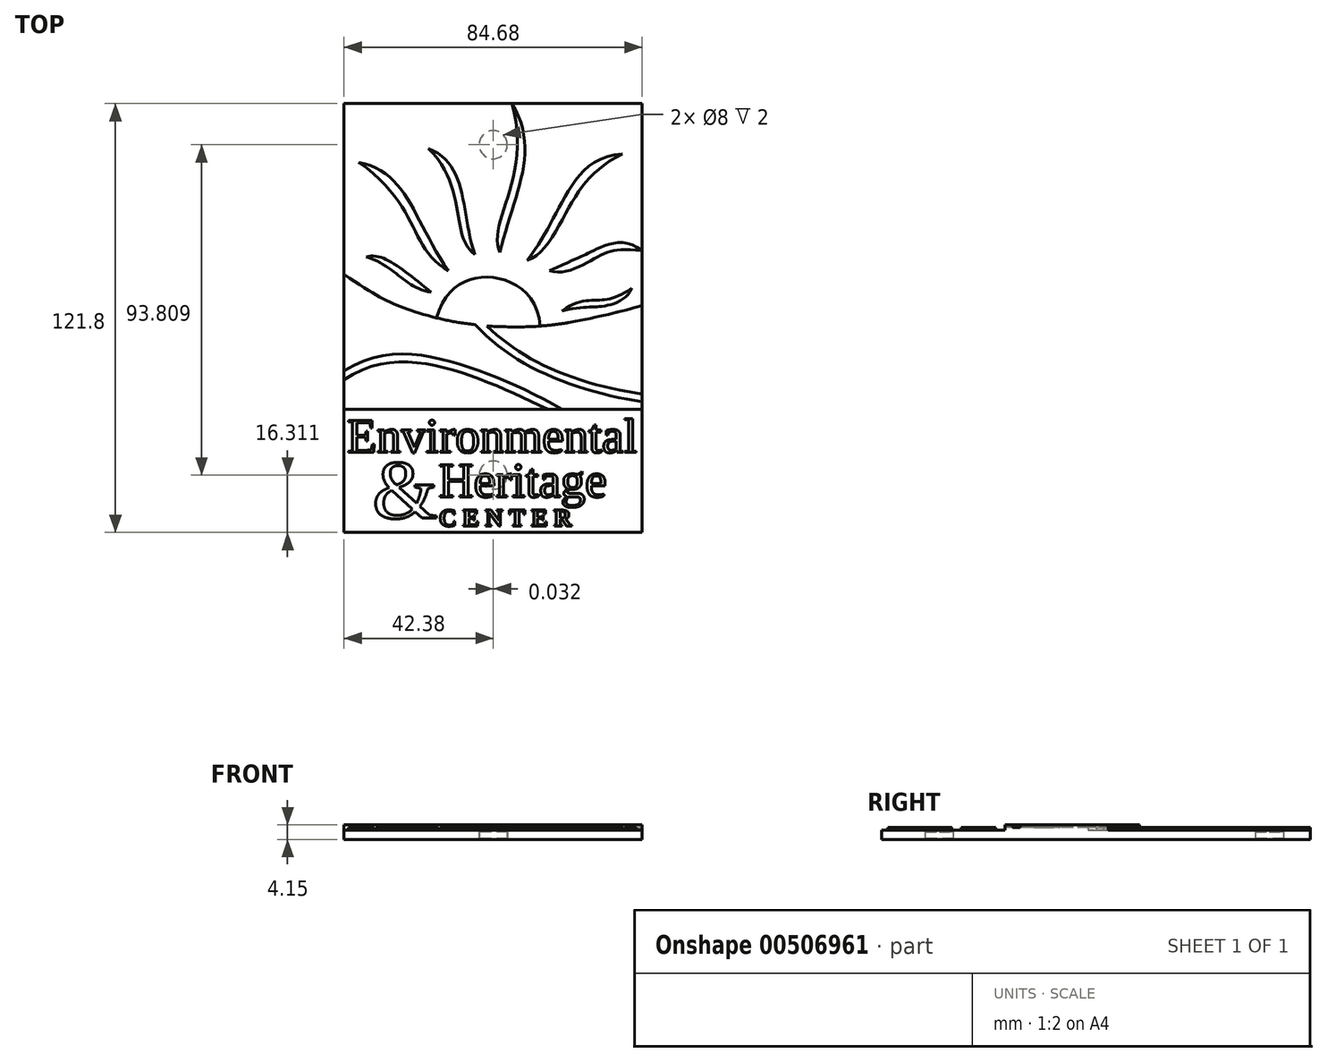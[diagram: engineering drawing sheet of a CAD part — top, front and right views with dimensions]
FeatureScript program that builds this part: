
annotation { "Feature Type Name" : "Feature", "Feature Type Description" : "" }
export const myFeature = defineFeature(function(context is Context, id is Id, definition is map)
    precondition{}
    {
        {
            var Q0;
            Q0=qCreatedBy(makeId("Top.planeOp"),FACE);
            var sketch = newSketch(context, id + "F0", { "sketchPlane" : qUnion([Q0])});
            skFitSpline(sketch, "E0", {"points": [v(8.38, 50.3) * mm, v(5.04, 8) * mm], "startDerivative": vector(25.7, -41) * mm, "endDerivative": vector(-10.42, -47.31) * mm});
            skFitSpline(sketch, "E1", {"points": [v(8.38, 50.3) * mm, v(5.04, 8) * mm], "startDerivative": vector(18.47, -60.9) * mm, "endDerivative": vector(12.18, -25) * mm});
            skFitSpline(sketch, "E2", {"points": [v(-15.3, 37.53) * mm, v(-2.15, 7.39) * mm], "startDerivative": vector(34.1, -13.29) * mm, "endDerivative": vector(12.15, -37.51) * mm});
            skFitSpline(sketch, "E3", {"points": [v(-15.3, 37.53) * mm, v(-2.15, 7.39) * mm], "startDerivative": vector(33.89, -33.1) * mm, "endDerivative": vector(21.74, -16.62) * mm});
            skFitSpline(sketch, "E4", {"points": [v(-35.08, 33.63) * mm, v(-9.6, 2.78) * mm], "startDerivative": vector(41.44, -7.64) * mm, "endDerivative": vector(29.77, -42.85) * mm});
            skFitSpline(sketch, "E5", {"points": [v(-35.08, 33.63) * mm, v(-9.6, 2.78) * mm], "startDerivative": vector(53.11, -37.62) * mm, "endDerivative": vector(34.6, -20.12) * mm});
            skFitSpline(sketch, "E6", {"points": [v(-32.93, 6.81) * mm, v(-14.52, -3.25) * mm], "startDerivative": vector(15.17, 4.31) * mm, "endDerivative": vector(22.51, -17.72) * mm});
            skFitSpline(sketch, "E7", {"points": [v(-32.93, 6.81) * mm, v(-14.52, -3.25) * mm], "startDerivative": vector(24.9, -7.82) * mm, "endDerivative": vector(22.51, -3.35) * mm});
            skFitSpline(sketch, "E8", {"points": [v(39.82, 36.01) * mm, v(22.83, 22.68) * mm, v(12.74, 5.78) * mm], "startDerivative": vector(-55.6, -3.28) * mm, "endDerivative": vector(-26.64, -34.5) * mm});
            skFitSpline(sketch, "E9", {"points": [v(39.82, 36.01) * mm, v(24.83, 21.19) * mm, v(12.74, 5.78) * mm], "startDerivative": vector(-45.9, -23.41) * mm, "endDerivative": vector(-32.14, -10) * mm});
            skFitSpline(sketch, "E10", {"points": [v(19.04, 2.84) * mm, v(30.94, 8.22) * mm, v(45.4, 8.53) * mm], "startDerivative": vector(51.65, 23.48) * mm, "endDerivative": vector(31, -26.2) * mm});
            skFitSpline(sketch, "E11", {"points": [v(19.04, 2.84) * mm, v(32.52, 6.63) * mm, v(45.4, 8.53) * mm], "startDerivative": vector(26.96, -9.36) * mm, "endDerivative": vector(42.76, -4.24) * mm});
            skFitSpline(sketch, "E12", {"points": [v(22.65, -8.56) * mm, v(33.15, -5.52) * mm, v(42.52, -2.16) * mm], "startDerivative": vector(26.71, 19.3) * mm, "endDerivative": vector(25.67, 16.34) * mm});
            skFitSpline(sketch, "E13", {"points": [v(22.65, -8.56) * mm, v(33.85, -7.3) * mm, v(42.52, -2.16) * mm], "startDerivative": vector(37.68, 8.5) * mm, "endDerivative": vector(10.55, 22.66) * mm});
            skFitSpline(sketch, "E14", {"points": [v(1.37, -12.89) * mm, v(18.9, -24.72) * mm, v(45.4, -32.17) * mm], "startDerivative": vector(30.87, -29.73) * mm, "endDerivative": vector(47.12, -6.3) * mm});
            skFitSpline(sketch, "E15", {"points": [v(-1.98, -12.48) * mm, v(18.34, -26.68) * mm, v(45.4, -34.32) * mm], "startDerivative": vector(34.69, -38) * mm, "endDerivative": vector(48.3, -6.34) * mm});
            skFitSpline(sketch, "E16", {"points": [v(1.37, -12.89) * mm, v(22.2, -12.25) * mm, v(45.48, -7.1) * mm], "startDerivative": vector(44.38, -2.18) * mm, "endDerivative": vector(34.77, 9.05) * mm});
            skFitSpline(sketch, "E17", {"points": [v(-39.29, -25.63) * mm, v(-8.43, -23.14) * mm, v(22.66, -36.5) * mm], "startDerivative": vector(63.24, 41.09) * mm, "endDerivative": vector(60.24, -34.22) * mm});
            skFitSpline(sketch, "E18", {"points": [v(-39.29, -28.2) * mm, v(-9.86, -24.95) * mm, v(18.67, -36.5) * mm], "startDerivative": vector(58.5, 40.42) * mm, "endDerivative": vector(56.35, -26.33) * mm});
            skFitSpline(sketch, "E19", {"points": [v(-39.29, 1.8) * mm, v(-21.77, -7.9) * mm, v(-1.98, -12.48) * mm], "startDerivative": vector(51.08, -34.3) * mm, "endDerivative": vector(42.59, -4.16) * mm});
            skFitSpline(sketch, "E20", {"points": [v(-12.98, -10.56) * mm, v(1.97, 1) * mm, v(16.44, -12.88) * mm], "startDerivative": vector(15.1, 52.69) * mm, "endDerivative": vector(3.95, -54.95) * mm});
            skLineSegment(sketch, "E21", {"start": v(-39.29, 50.3) * mm, "end": v(-39.29, -36.5) * mm});
            skLineSegment(sketch, "E22", {"start": v(-39.29, 50.3) * mm, "end": v(45.4, 50.3) * mm});
            skLineSegment(sketch, "E23", {"start": v(-39.29, -36.5) * mm, "end": v(45.4, -36.5) * mm});
            skLineSegment(sketch, "E24.trimOffspring", {"start": v(42.48, 8.76) * mm, "end": v(42.48, 8.78) * mm});
            skLineSegment(sketch, "E25", {"start": v(45.4, 50.3) * mm, "end": v(45.4, -36.5) * mm});
            skText(sketch, "E26", { "text": "Environmental", "fontName": "Tinos-Regular.ttf"});
            skText(sketch, "E27", { "text": "Heritage", "fontName": "Tinos-Regular.ttf"});
            skText(sketch, "E28", { "text": "C E N T E R", "fontName": "Tinos-Bold.ttf"});
            skText(sketch, "E29", { "text": "&", "fontName": "Tinos-Regular.ttf"});
            skLineSegment(sketch, "E30", {"start": v(3.05, 50.3) * mm, "end": v(3.05, -36.5) * mm, "construction": true});
            skLineSegment(sketch, "E31", {"start": v(-39.29, -36.5) * mm, "end": v(-39.29, -71.5) * mm});
            skLineSegment(sketch, "E32", {"start": v(45.4, -36.5) * mm, "end": v(45.4, -71.5) * mm});
            skLineSegment(sketch, "E33", {"start": v(-39.29, -71.5) * mm, "end": v(45.4, -71.5) * mm});
            const initialGuessF0  = {"E26": [-0.0385, -0.04877, 1, 0, 0.01], "E27": [-0.01243, -0.06139, 1, 0, 0.01], "E28": [-0.0123, -0.06969, 1, 0, 0.005], "E29": [-0.0312, -0.06742, 1, 0, 0.01715]};
            skSetInitialGuess(sketch, initialGuessF0);
            skSolve(sketch);
        }
        {
            var Q0;
            Q0 = qSketchRegion(id + "F0", true);
            var Q1;
            Q1=makeQuery(id+"F0.imprint","IMPRINT",FACE,{"disambiguationData":[TD([[makeQuery(id+"F0.imprint","IMPRINT",EDGE,{"derivedFrom":sQuery(id+"F0.wireOp",EDGE,"E6")}),-1.0]])]});
            var Q2;
            Q2=makeQuery(id+"F0.imprint","IMPRINT",FACE,{"disambiguationData":[TD([[makeQuery(id+"F0.imprint","IMPRINT",EDGE,{"derivedFrom":sQuery(id+"F0.wireOp",EDGE,"E4")}),-1.0]])]});
            var Q3;
            Q3=makeQuery(id+"F0.imprint","IMPRINT",FACE,{"disambiguationData":[TD([[makeQuery(id+"F0.imprint","IMPRINT",EDGE,{"derivedFrom":sQuery(id+"F0.wireOp",EDGE,"E2")}),-1.0]])]});
            var Q4;
            Q4=makeQuery(id+"F0.imprint","IMPRINT",FACE,{"disambiguationData":[TD([[makeQuery(id+"F0.imprint","IMPRINT",EDGE,{"derivedFrom":sQuery(id+"F0.wireOp",EDGE,"E8")}),1.0]])]});
            var Q5;
            Q5=makeQuery(id+"F0.imprint","IMPRINT",FACE,{"disambiguationData":[TD([[makeQuery(id+"F0.imprint","IMPRINT",EDGE,{"derivedFrom":sQuery(id+"F0.wireOp",EDGE,"E12")}),-1.0]])]});
            var Q6;
            {var subQ0=sQuery(id+"F0.wireOp",EDGE,"E1");Q6=makeQuery(id+"F0.imprint","IMPRINT",FACE,{"disambiguationData":[TD([[makeQuery(id+"F0.imprint","IMPRINT",EDGE,{"derivedFrom":subQ0}),1.0]])]});}
            var Q7;
            Q7=makeQuery(id+"F0.imprint","IMPRINT",FACE,{"disambiguationData":[TD([[makeQuery(id+"F0.imprint","IMPRINT",EDGE,{"derivedFrom":sQuery(id+"F0.wireOp",EDGE,"E29.sketch_text.stroke-28")}),1.0]])]});
            var Q8;
            Q8=makeQuery(id+"F0.imprint","IMPRINT",FACE,{"disambiguationData":[TD([[makeQuery(id+"F0.imprint","IMPRINT",EDGE,{"derivedFrom":sQuery(id+"F0.wireOp",EDGE,"E26.sketch_text.stroke-0")}),-1.0]])]});
            var Q9;
            Q9=makeQuery(id+"F0.imprint","IMPRINT",FACE,{"disambiguationData":[TD([[makeQuery(id+"F0.imprint","IMPRINT",EDGE,{"derivedFrom":sQuery(id+"F0.wireOp",EDGE,"E26.sketch_text.stroke-26")}),-1.0]])]});
            var Q10;
            Q10=makeQuery(id+"F0.imprint","IMPRINT",FACE,{"disambiguationData":[TD([[makeQuery(id+"F0.imprint","IMPRINT",EDGE,{"derivedFrom":sQuery(id+"F0.wireOp",EDGE,"E26.sketch_text.stroke-51")}),-1.0]])]});
            var Q11;
            Q11=makeQuery(id+"F0.imprint","IMPRINT",FACE,{"disambiguationData":[TD([[makeQuery(id+"F0.imprint","IMPRINT",EDGE,{"derivedFrom":sQuery(id+"F0.wireOp",EDGE,"E26.sketch_text.stroke-74")}),-1.0]])]});
            var Q12;
            Q12=makeQuery(id+"F0.imprint","IMPRINT",FACE,{"disambiguationData":[TD([[makeQuery(id+"F0.imprint","IMPRINT",EDGE,{"derivedFrom":sQuery(id+"F0.wireOp",EDGE,"E26.sketch_text.stroke-84")}),-1.0]])]});
            var Q13;
            Q13=makeQuery(id+"F0.imprint","IMPRINT",FACE,{"disambiguationData":[TD([[makeQuery(id+"F0.imprint","IMPRINT",EDGE,{"derivedFrom":sQuery(id+"F0.wireOp",EDGE,"E26.sketch_text.stroke-103")}),-1.0]])]});
            var Q14;
            Q14=makeQuery(id+"F0.imprint","IMPRINT",FACE,{"disambiguationData":[TD([[makeQuery(id+"F0.imprint","IMPRINT",EDGE,{"derivedFrom":sQuery(id+"F0.wireOp",EDGE,"E26.sketch_text.stroke-110")}),1.0]])]});
            var Q15;
            Q15=makeQuery(id+"F0.imprint","IMPRINT",FACE,{"disambiguationData":[TD([[makeQuery(id+"F0.imprint","IMPRINT",EDGE,{"derivedFrom":sQuery(id+"F0.wireOp",EDGE,"E26.sketch_text.stroke-118")}),-1.0]])]});
            var Q16;
            Q16=makeQuery(id+"F0.imprint","IMPRINT",FACE,{"disambiguationData":[TD([[makeQuery(id+"F0.imprint","IMPRINT",EDGE,{"derivedFrom":sQuery(id+"F0.wireOp",EDGE,"E26.sketch_text.stroke-143")}),-1.0]])]});
            var Q17;
            Q17=makeQuery(id+"F0.imprint","IMPRINT",FACE,{"disambiguationData":[TD([[makeQuery(id+"F0.imprint","IMPRINT",EDGE,{"derivedFrom":sQuery(id+"F0.wireOp",EDGE,"E27.sketch_text.stroke-49")}),-1.0]])]});
            var Q18;
            Q18=makeQuery(id+"F0.imprint","IMPRINT",FACE,{"disambiguationData":[TD([[makeQuery(id+"F0.imprint","IMPRINT",EDGE,{"derivedFrom":sQuery(id+"F0.wireOp",EDGE,"E27.sketch_text.stroke-28")}),-1.0]])]});
            var Q19;
            Q19=makeQuery(id+"F0.imprint","IMPRINT",FACE,{"disambiguationData":[TD([[makeQuery(id+"F0.imprint","IMPRINT",EDGE,{"derivedFrom":sQuery(id+"F0.wireOp",EDGE,"E27.sketch_text.stroke-44")}),1.0]])]});
            var Q20;
            Q20=makeQuery(id+"F0.imprint","IMPRINT",FACE,{"disambiguationData":[TD([[makeQuery(id+"F0.imprint","IMPRINT",EDGE,{"derivedFrom":sQuery(id+"F0.wireOp",EDGE,"E27.sketch_text.stroke-0")}),-1.0]])]});
            var Q21;
            Q21=makeQuery(id+"F0.imprint","IMPRINT",FACE,{"disambiguationData":[TD([[makeQuery(id+"F0.imprint","IMPRINT",EDGE,{"derivedFrom":sQuery(id+"F0.wireOp",EDGE,"E29.sketch_text.stroke-0")}),-1.0]])]});
            var Q22;
            Q22=makeQuery(id+"F0.imprint","IMPRINT",FACE,{"disambiguationData":[TD([[makeQuery(id+"F0.imprint","IMPRINT",EDGE,{"derivedFrom":sQuery(id+"F0.wireOp",EDGE,"E29.sketch_text.stroke-34")}),1.0]])]});
            var Q23;
            Q23=makeQuery(id+"F0.imprint","IMPRINT",FACE,{"disambiguationData":[TD([[makeQuery(id+"F0.imprint","IMPRINT",EDGE,{"derivedFrom":sQuery(id+"F0.wireOp",EDGE,"E28.sketch_text.stroke-0")}),-1.0]])]});
            var Q24;
            Q24=makeQuery(id+"F0.imprint","IMPRINT",FACE,{"disambiguationData":[TD([[makeQuery(id+"F0.imprint","IMPRINT",EDGE,{"derivedFrom":sQuery(id+"F0.wireOp",EDGE,"E28.sketch_text.stroke-20")}),-1.0]])]});
            var Q25;
            Q25=makeQuery(id+"F0.imprint","IMPRINT",FACE,{"disambiguationData":[TD([[makeQuery(id+"F0.imprint","IMPRINT",EDGE,{"derivedFrom":sQuery(id+"F0.wireOp",EDGE,"E28.sketch_text.stroke-46")}),-1.0]])]});
            var Q26;
            Q26=makeQuery(id+"F0.imprint","IMPRINT",FACE,{"disambiguationData":[TD([[makeQuery(id+"F0.imprint","IMPRINT",EDGE,{"derivedFrom":sQuery(id+"F0.wireOp",EDGE,"E28.sketch_text.stroke-66")}),-1.0]])]});
            var Q27;
            Q27=makeQuery(id+"F0.imprint","IMPRINT",FACE,{"disambiguationData":[TD([[makeQuery(id+"F0.imprint","IMPRINT",EDGE,{"derivedFrom":sQuery(id+"F0.wireOp",EDGE,"E27.sketch_text.stroke-76")}),-1.0]])]});
            var Q28;
            Q28=makeQuery(id+"F0.imprint","IMPRINT",FACE,{"disambiguationData":[TD([[makeQuery(id+"F0.imprint","IMPRINT",EDGE,{"derivedFrom":sQuery(id+"F0.wireOp",EDGE,"E27.sketch_text.stroke-68")}),-1.0]])]});
            var Q29;
            Q29=makeQuery(id+"F0.imprint","IMPRINT",FACE,{"disambiguationData":[TD([[makeQuery(id+"F0.imprint","IMPRINT",EDGE,{"derivedFrom":sQuery(id+"F0.wireOp",EDGE,"E26.sketch_text.stroke-66")}),-1.0]])]});
            var Q30;
            Q30=makeQuery(id+"F0.imprint","IMPRINT",FACE,{"disambiguationData":[TD([[makeQuery(id+"F0.imprint","IMPRINT",EDGE,{"derivedFrom":sQuery(id+"F0.wireOp",EDGE,"E26.sketch_text.stroke-184")}),-1.0]])]});
            var Q31;
            Q31=makeQuery(id+"F0.imprint","IMPRINT",FACE,{"disambiguationData":[TD([[makeQuery(id+"F0.imprint","IMPRINT",EDGE,{"derivedFrom":sQuery(id+"F0.wireOp",EDGE,"E26.sketch_text.stroke-200")}),1.0]])]});
            var Q32;
            Q32=makeQuery(id+"F0.imprint","IMPRINT",FACE,{"disambiguationData":[TD([[makeQuery(id+"F0.imprint","IMPRINT",EDGE,{"derivedFrom":sQuery(id+"F0.wireOp",EDGE,"E26.sketch_text.stroke-205")}),-1.0]])]});
            var Q33;
            Q33=makeQuery(id+"F0.imprint","IMPRINT",FACE,{"disambiguationData":[TD([[makeQuery(id+"F0.imprint","IMPRINT",EDGE,{"derivedFrom":sQuery(id+"F0.wireOp",EDGE,"E26.sketch_text.stroke-230")}),-1.0]])]});
            var Q34;
            Q34=makeQuery(id+"F0.imprint","IMPRINT",FACE,{"disambiguationData":[TD([[makeQuery(id+"F0.imprint","IMPRINT",EDGE,{"derivedFrom":sQuery(id+"F0.wireOp",EDGE,"E26.sketch_text.stroke-270")}),1.0]])]});
            var Q35;
            Q35=makeQuery(id+"F0.imprint","IMPRINT",FACE,{"disambiguationData":[TD([[makeQuery(id+"F0.imprint","IMPRINT",EDGE,{"derivedFrom":sQuery(id+"F0.wireOp",EDGE,"E26.sketch_text.stroke-249")}),-1.0]])]});
            var Q36;
            Q36=makeQuery(id+"F0.imprint","IMPRINT",FACE,{"disambiguationData":[TD([[makeQuery(id+"F0.imprint","IMPRINT",EDGE,{"derivedFrom":sQuery(id+"F0.wireOp",EDGE,"E26.sketch_text.stroke-277")}),-1.0]])]});
            var Q37;
            Q37=makeQuery(id+"F0.imprint","IMPRINT",FACE,{"disambiguationData":[TD([[makeQuery(id+"F0.imprint","IMPRINT",EDGE,{"derivedFrom":sQuery(id+"F0.wireOp",EDGE,"E27.sketch_text.stroke-178")}),-1.0]])]});
            var Q38;
            Q38=makeQuery(id+"F0.imprint","IMPRINT",FACE,{"disambiguationData":[TD([[makeQuery(id+"F0.imprint","IMPRINT",EDGE,{"derivedFrom":sQuery(id+"F0.wireOp",EDGE,"E27.sketch_text.stroke-194")}),1.0]])]});
            var Q39;
            Q39=makeQuery(id+"F0.imprint","IMPRINT",FACE,{"disambiguationData":[TD([[makeQuery(id+"F0.imprint","IMPRINT",EDGE,{"derivedFrom":sQuery(id+"F0.wireOp",EDGE,"E27.sketch_text.stroke-133")}),-1.0]])]});
            var Q40;
            Q40=makeQuery(id+"F0.imprint","IMPRINT",FACE,{"disambiguationData":[TD([[makeQuery(id+"F0.imprint","IMPRINT",EDGE,{"derivedFrom":sQuery(id+"F0.wireOp",EDGE,"E27.sketch_text.stroke-170")}),1.0]])]});
            var Q41;
            Q41=makeQuery(id+"F0.imprint","IMPRINT",FACE,{"disambiguationData":[TD([[makeQuery(id+"F0.imprint","IMPRINT",EDGE,{"derivedFrom":sQuery(id+"F0.wireOp",EDGE,"E27.sketch_text.stroke-161")}),1.0]])]});
            var Q42;
            Q42=makeQuery(id+"F0.imprint","IMPRINT",FACE,{"disambiguationData":[TD([[makeQuery(id+"F0.imprint","IMPRINT",EDGE,{"derivedFrom":sQuery(id+"F0.wireOp",EDGE,"E27.sketch_text.stroke-126")}),1.0]])]});
            var Q43;
            Q43=makeQuery(id+"F0.imprint","IMPRINT",FACE,{"disambiguationData":[TD([[makeQuery(id+"F0.imprint","IMPRINT",EDGE,{"derivedFrom":sQuery(id+"F0.wireOp",EDGE,"E27.sketch_text.stroke-105")}),-1.0]])]});
            var Q44;
            Q44=makeQuery(id+"F0.imprint","IMPRINT",FACE,{"disambiguationData":[TD([[makeQuery(id+"F0.imprint","IMPRINT",EDGE,{"derivedFrom":sQuery(id+"F0.wireOp",EDGE,"E27.sketch_text.stroke-86")}),-1.0]])]});
            var Q45;
            Q45=makeQuery(id+"F0.imprint","IMPRINT",FACE,{"disambiguationData":[TD([[makeQuery(id+"F0.imprint","IMPRINT",EDGE,{"derivedFrom":sQuery(id+"F0.wireOp",EDGE,"E28.sketch_text.stroke-84")}),-1.0]])]});
            var Q46;
            Q46=makeQuery(id+"F0.imprint","IMPRINT",FACE,{"disambiguationData":[TD([[makeQuery(id+"F0.imprint","IMPRINT",EDGE,{"derivedFrom":sQuery(id+"F0.wireOp",EDGE,"E28.sketch_text.stroke-110")}),-1.0]])]});
            var Q47;
            Q47=makeQuery(id+"F0.imprint","IMPRINT",FACE,{"disambiguationData":[TD([[makeQuery(id+"F0.imprint","IMPRINT",EDGE,{"derivedFrom":sQuery(id+"F0.wireOp",EDGE,"E28.sketch_text.stroke-129")}),1.0]])]});
            extrude(context, id + "F1", {"entities" : qUnion([Q0, Q1, Q2, Q3, Q4, Q5, Q6, Q7, Q8, Q9, Q10, Q11, Q12, Q13, Q14, Q15, Q16, Q17, Q18, Q19, Q20, Q21, Q22, Q23, Q24, Q25, Q26, Q27, Q28, Q29, Q30, Q31, Q32, Q33, Q34, Q35, Q36, Q37, Q38, Q39, Q40, Q41, Q42, Q43, Q44, Q45, Q46, Q47]), "depth" : 2.55 * mm, "offsetDistance" : 25 * mm});
        }
        {
            var Q0;
            Q0=makeQuery(id+"F1.opExtrude","CAP_FACE",FACE,{"disambiguationData":[OSD([sQuery(id+"F0.wireOp",EDGE,"E21"),sQuery(id+"F0.wireOp",EDGE,"E22"),sQuery(id+"F0.wireOp",EDGE,"E25"),sQuery(id+"F0.wireOp",EDGE,"E31"),sQuery(id+"F0.wireOp",EDGE,"E32"),sQuery(id+"F0.wireOp",EDGE,"E33")])],"isStart":false});
            var sketch = newSketch(context, id + "F2", { "sketchPlane" : qUnion([Q0])});
            skFitSpline(sketch, "E34", {"points": [v(8.38, 50.3) * mm, v(5.04, 8) * mm], "startDerivative": vector(25.7, -41) * mm, "endDerivative": vector(-10.42, -47.31) * mm});
            skFitSpline(sketch, "E35", {"points": [v(8.38, 50.3) * mm, v(5.04, 8) * mm], "startDerivative": vector(18.47, -60.9) * mm, "endDerivative": vector(12.18, -25) * mm});
            skFitSpline(sketch, "E36", {"points": [v(-15.3, 37.53) * mm, v(-2.15, 7.39) * mm], "startDerivative": vector(34.1, -13.29) * mm, "endDerivative": vector(12.15, -37.51) * mm});
            skFitSpline(sketch, "E37", {"points": [v(-15.3, 37.53) * mm, v(-2.15, 7.39) * mm], "startDerivative": vector(33.89, -33.1) * mm, "endDerivative": vector(21.74, -16.62) * mm});
            skFitSpline(sketch, "E38", {"points": [v(-35.08, 33.63) * mm, v(-9.6, 2.78) * mm], "startDerivative": vector(41.44, -7.64) * mm, "endDerivative": vector(29.77, -42.85) * mm});
            skFitSpline(sketch, "E39", {"points": [v(-35.08, 33.63) * mm, v(-9.6, 2.78) * mm], "startDerivative": vector(53.11, -37.62) * mm, "endDerivative": vector(34.6, -20.12) * mm});
            skFitSpline(sketch, "E40", {"points": [v(-32.93, 6.81) * mm, v(-14.52, -3.25) * mm], "startDerivative": vector(15.17, 4.31) * mm, "endDerivative": vector(22.51, -17.72) * mm});
            skFitSpline(sketch, "E41", {"points": [v(-32.93, 6.81) * mm, v(-14.52, -3.25) * mm], "startDerivative": vector(24.9, -7.82) * mm, "endDerivative": vector(22.51, -3.35) * mm});
            skFitSpline(sketch, "E42", {"points": [v(39.82, 36.01) * mm, v(22.83, 22.68) * mm, v(12.74, 5.78) * mm], "startDerivative": vector(-55.6, -3.28) * mm, "endDerivative": vector(-26.64, -34.5) * mm});
            skFitSpline(sketch, "E43", {"points": [v(39.82, 36.01) * mm, v(24.83, 21.19) * mm, v(12.74, 5.78) * mm], "startDerivative": vector(-45.9, -23.41) * mm, "endDerivative": vector(-32.14, -10) * mm});
            skFitSpline(sketch, "E44", {"points": [v(19.04, 2.84) * mm, v(30.94, 8.22) * mm, v(45.38, 8.52) * mm], "startDerivative": vector(51.65, 23.48) * mm, "endDerivative": vector(31, -26.2) * mm});
            skFitSpline(sketch, "E45", {"points": [v(19.04, 2.84) * mm, v(32.52, 6.63) * mm, v(45.38, 8.53) * mm], "startDerivative": vector(26.96, -9.36) * mm, "endDerivative": vector(42.76, -4.23) * mm});
            skFitSpline(sketch, "E46", {"points": [v(22.65, -8.56) * mm, v(33.15, -5.52) * mm, v(42.52, -2.16) * mm], "startDerivative": vector(26.71, 19.3) * mm, "endDerivative": vector(25.67, 16.34) * mm});
            skFitSpline(sketch, "E47", {"points": [v(22.65, -8.56) * mm, v(33.85, -7.3) * mm, v(42.52, -2.16) * mm], "startDerivative": vector(37.68, 8.5) * mm, "endDerivative": vector(10.55, 22.66) * mm});
            skFitSpline(sketch, "E48", {"points": [v(1.37, -12.89) * mm, v(18.9, -24.72) * mm, v(45.4, -32.17) * mm], "startDerivative": vector(30.87, -29.73) * mm, "endDerivative": vector(47.12, -6.3) * mm});
            skFitSpline(sketch, "E49", {"points": [v(-1.98, -12.48) * mm, v(18.34, -26.68) * mm, v(45.4, -34.32) * mm], "startDerivative": vector(34.69, -38) * mm, "endDerivative": vector(48.3, -6.34) * mm});
            skFitSpline(sketch, "E50", {"points": [v(1.37, -12.89) * mm, v(22.2, -12.25) * mm, v(45.48, -7.1) * mm], "startDerivative": vector(44.38, -2.18) * mm, "endDerivative": vector(34.77, 9.05) * mm});
            skFitSpline(sketch, "E51", {"points": [v(-39.29, -25.63) * mm, v(-8.43, -23.14) * mm, v(22.66, -36.5) * mm], "startDerivative": vector(63.24, 41.09) * mm, "endDerivative": vector(60.24, -34.22) * mm});
            skFitSpline(sketch, "E52", {"points": [v(-39.29, -28.2) * mm, v(-9.86, -24.95) * mm, v(18.67, -36.5) * mm], "startDerivative": vector(58.5, 40.42) * mm, "endDerivative": vector(56.35, -26.33) * mm});
            skFitSpline(sketch, "E53", {"points": [v(-39.29, 1.8) * mm, v(-21.77, -7.9) * mm, v(-1.98, -12.48) * mm], "startDerivative": vector(51.08, -34.3) * mm, "endDerivative": vector(42.59, -4.16) * mm});
            skFitSpline(sketch, "E54", {"points": [v(-12.98, -10.56) * mm, v(1.97, 1) * mm, v(16.44, -12.88) * mm], "startDerivative": vector(15.1, 52.69) * mm, "endDerivative": vector(3.95, -54.95) * mm});
            skLineSegment(sketch, "E55", {"start": v(-39.29, 50.3) * mm, "end": v(-39.29, -36.5) * mm});
            skLineSegment(sketch, "E56", {"start": v(-39.29, 50.3) * mm, "end": v(45.4, 50.3) * mm});
            skLineSegment(sketch, "E57", {"start": v(-39.29, -36.5) * mm, "end": v(45.4, -36.5) * mm});
            skLineSegment(sketch, "E58.trimOffspring", {"start": v(42.48, 8.76) * mm, "end": v(42.48, 8.78) * mm});
            skLineSegment(sketch, "E59", {"start": v(45.4, 50.3) * mm, "end": v(45.4, -36.5) * mm});
            skText(sketch, "E60", { "text": "Environmental", "fontName": "Tinos-Regular.ttf"});
            skText(sketch, "E61", { "text": "Heritage", "fontName": "Tinos-Regular.ttf"});
            skText(sketch, "E62", { "text": "C E N T E R", "fontName": "Tinos-Bold.ttf"});
            skText(sketch, "E63", { "text": "&", "fontName": "Tinos-Regular.ttf"});
            skLineSegment(sketch, "E64", {"start": v(3.05, 50.3) * mm, "end": v(3.05, -36.5) * mm, "construction": true});
            skLineSegment(sketch, "E65", {"start": v(-39.29, -36.5) * mm, "end": v(-39.29, -71.5) * mm});
            skLineSegment(sketch, "E66", {"start": v(45.4, -36.5) * mm, "end": v(45.4, -71.5) * mm});
            skLineSegment(sketch, "E67", {"start": v(-39.29, -71.5) * mm, "end": v(45.4, -71.5) * mm});
            const initialGuessF2  = {"E60": [-0.0385, -0.04877, 1, 0, 0.01], "E61": [-0.01243, -0.06139, 1, 0, 0.01], "E62": [-0.0123, -0.06969, 1, 0, 0.005], "E63": [-0.0312, -0.06742, 1, 0, 0.01715]};
            skSetInitialGuess(sketch, initialGuessF2);
            skSolve(sketch);
        }
        {
            var Q0;
            Q0=makeQuery(id+"F2.imprint","IMPRINT",FACE,{"disambiguationData":[TD([[makeQuery(id+"F2.imprint","IMPRINT",EDGE,{"derivedFrom":sQuery(id+"F2.wireOp",EDGE,"E60.sketch_text.stroke-205")}),-1.0]])]});
            var Q1;
            Q1=makeQuery(id+"F2.imprint","IMPRINT",FACE,{"disambiguationData":[TD([[makeQuery(id+"F2.imprint","IMPRINT",EDGE,{"derivedFrom":sQuery(id+"F2.wireOp",EDGE,"E60.sketch_text.stroke-184")}),-1.0]])]});
            var Q2;
            Q2=makeQuery(id+"F2.imprint","IMPRINT",FACE,{"disambiguationData":[TD([[makeQuery(id+"F2.imprint","IMPRINT",EDGE,{"derivedFrom":sQuery(id+"F2.wireOp",EDGE,"E60.sketch_text.stroke-143")}),-1.0]])]});
            var Q3;
            Q3=makeQuery(id+"F2.imprint","IMPRINT",FACE,{"disambiguationData":[TD([[makeQuery(id+"F2.imprint","IMPRINT",EDGE,{"derivedFrom":sQuery(id+"F2.wireOp",EDGE,"E60.sketch_text.stroke-118")}),-1.0]])]});
            var Q4;
            Q4=makeQuery(id+"F2.imprint","IMPRINT",FACE,{"disambiguationData":[TD([[makeQuery(id+"F2.imprint","IMPRINT",EDGE,{"derivedFrom":sQuery(id+"F2.wireOp",EDGE,"E60.sketch_text.stroke-103")}),-1.0]])]});
            var Q5;
            Q5=makeQuery(id+"F2.imprint","IMPRINT",FACE,{"disambiguationData":[TD([[makeQuery(id+"F2.imprint","IMPRINT",EDGE,{"derivedFrom":sQuery(id+"F2.wireOp",EDGE,"E60.sketch_text.stroke-84")}),-1.0]])]});
            var Q6;
            Q6=makeQuery(id+"F2.imprint","IMPRINT",FACE,{"disambiguationData":[TD([[makeQuery(id+"F2.imprint","IMPRINT",EDGE,{"derivedFrom":sQuery(id+"F2.wireOp",EDGE,"E60.sketch_text.stroke-230")}),-1.0]])]});
            var Q7;
            Q7=makeQuery(id+"F2.imprint","IMPRINT",FACE,{"disambiguationData":[TD([[makeQuery(id+"F2.imprint","IMPRINT",EDGE,{"derivedFrom":sQuery(id+"F2.wireOp",EDGE,"E60.sketch_text.stroke-249")}),-1.0]])]});
            var Q8;
            Q8=makeQuery(id+"F2.imprint","IMPRINT",FACE,{"disambiguationData":[TD([[makeQuery(id+"F2.imprint","IMPRINT",EDGE,{"derivedFrom":sQuery(id+"F2.wireOp",EDGE,"E60.sketch_text.stroke-277")}),-1.0]])]});
            var Q9;
            Q9=makeQuery(id+"F2.imprint","IMPRINT",FACE,{"disambiguationData":[TD([[makeQuery(id+"F2.imprint","IMPRINT",EDGE,{"derivedFrom":sQuery(id+"F2.wireOp",EDGE,"E61.sketch_text.stroke-178")}),-1.0]])]});
            var Q10;
            Q10=makeQuery(id+"F2.imprint","IMPRINT",FACE,{"disambiguationData":[TD([[makeQuery(id+"F2.imprint","IMPRINT",EDGE,{"derivedFrom":sQuery(id+"F2.wireOp",EDGE,"E61.sketch_text.stroke-133")}),-1.0]])]});
            var Q11;
            Q11=makeQuery(id+"F2.imprint","IMPRINT",FACE,{"disambiguationData":[TD([[makeQuery(id+"F2.imprint","IMPRINT",EDGE,{"derivedFrom":sQuery(id+"F2.wireOp",EDGE,"E61.sketch_text.stroke-105")}),-1.0]])]});
            var Q12;
            Q12=makeQuery(id+"F2.imprint","IMPRINT",FACE,{"disambiguationData":[TD([[makeQuery(id+"F2.imprint","IMPRINT",EDGE,{"derivedFrom":sQuery(id+"F2.wireOp",EDGE,"E61.sketch_text.stroke-86")}),-1.0]])]});
            var Q13;
            Q13=makeQuery(id+"F2.imprint","IMPRINT",FACE,{"disambiguationData":[TD([[makeQuery(id+"F2.imprint","IMPRINT",EDGE,{"derivedFrom":sQuery(id+"F2.wireOp",EDGE,"E61.sketch_text.stroke-76")}),-1.0]])]});
            var Q14;
            Q14=makeQuery(id+"F2.imprint","IMPRINT",FACE,{"disambiguationData":[TD([[makeQuery(id+"F2.imprint","IMPRINT",EDGE,{"derivedFrom":sQuery(id+"F2.wireOp",EDGE,"E61.sketch_text.stroke-68")}),-1.0]])]});
            var Q15;
            Q15=makeQuery(id+"F2.imprint","IMPRINT",FACE,{"disambiguationData":[TD([[makeQuery(id+"F2.imprint","IMPRINT",EDGE,{"derivedFrom":sQuery(id+"F2.wireOp",EDGE,"E61.sketch_text.stroke-49")}),-1.0]])]});
            var Q16;
            Q16=makeQuery(id+"F2.imprint","IMPRINT",FACE,{"disambiguationData":[TD([[makeQuery(id+"F2.imprint","IMPRINT",EDGE,{"derivedFrom":sQuery(id+"F2.wireOp",EDGE,"E61.sketch_text.stroke-28")}),-1.0]])]});
            var Q17;
            Q17=makeQuery(id+"F2.imprint","IMPRINT",FACE,{"disambiguationData":[TD([[makeQuery(id+"F2.imprint","IMPRINT",EDGE,{"derivedFrom":sQuery(id+"F2.wireOp",EDGE,"E61.sketch_text.stroke-0")}),-1.0]])]});
            var Q18;
            Q18=makeQuery(id+"F2.imprint","IMPRINT",FACE,{"disambiguationData":[TD([[makeQuery(id+"F2.imprint","IMPRINT",EDGE,{"derivedFrom":sQuery(id+"F2.wireOp",EDGE,"E62.sketch_text.stroke-0")}),-1.0]])]});
            var Q19;
            Q19=makeQuery(id+"F2.imprint","IMPRINT",FACE,{"disambiguationData":[TD([[makeQuery(id+"F2.imprint","IMPRINT",EDGE,{"derivedFrom":sQuery(id+"F2.wireOp",EDGE,"E62.sketch_text.stroke-20")}),-1.0]])]});
            var Q20;
            Q20=makeQuery(id+"F2.imprint","IMPRINT",FACE,{"disambiguationData":[TD([[makeQuery(id+"F2.imprint","IMPRINT",EDGE,{"derivedFrom":sQuery(id+"F2.wireOp",EDGE,"E62.sketch_text.stroke-46")}),-1.0]])]});
            var Q21;
            Q21=makeQuery(id+"F2.imprint","IMPRINT",FACE,{"disambiguationData":[TD([[makeQuery(id+"F2.imprint","IMPRINT",EDGE,{"derivedFrom":sQuery(id+"F2.wireOp",EDGE,"E62.sketch_text.stroke-66")}),-1.0]])]});
            var Q22;
            Q22=makeQuery(id+"F2.imprint","IMPRINT",FACE,{"disambiguationData":[TD([[makeQuery(id+"F2.imprint","IMPRINT",EDGE,{"derivedFrom":sQuery(id+"F2.wireOp",EDGE,"E63.sketch_text.stroke-0")}),-1.0]])]});
            var Q23;
            Q23=makeQuery(id+"F2.imprint","IMPRINT",FACE,{"disambiguationData":[TD([[makeQuery(id+"F2.imprint","IMPRINT",EDGE,{"derivedFrom":sQuery(id+"F2.wireOp",EDGE,"E60.sketch_text.stroke-74")}),-1.0]])]});
            var Q24;
            Q24=makeQuery(id+"F2.imprint","IMPRINT",FACE,{"disambiguationData":[TD([[makeQuery(id+"F2.imprint","IMPRINT",EDGE,{"derivedFrom":sQuery(id+"F2.wireOp",EDGE,"E60.sketch_text.stroke-51")}),-1.0]])]});
            var Q25;
            Q25=makeQuery(id+"F2.imprint","IMPRINT",FACE,{"disambiguationData":[TD([[makeQuery(id+"F2.imprint","IMPRINT",EDGE,{"derivedFrom":sQuery(id+"F2.wireOp",EDGE,"E62.sketch_text.stroke-84")}),-1.0]])]});
            var Q26;
            Q26=makeQuery(id+"F2.imprint","IMPRINT",FACE,{"disambiguationData":[TD([[makeQuery(id+"F2.imprint","IMPRINT",EDGE,{"derivedFrom":sQuery(id+"F2.wireOp",EDGE,"E60.sketch_text.stroke-0")}),-1.0]])]});
            var Q27;
            Q27=makeQuery(id+"F2.imprint","IMPRINT",FACE,{"disambiguationData":[TD([[makeQuery(id+"F2.imprint","IMPRINT",EDGE,{"derivedFrom":sQuery(id+"F2.wireOp",EDGE,"E60.sketch_text.stroke-26")}),-1.0]])]});
            var Q28;
            Q28=makeQuery(id+"F2.imprint","IMPRINT",FACE,{"disambiguationData":[TD([[makeQuery(id+"F2.imprint","IMPRINT",EDGE,{"derivedFrom":sQuery(id+"F2.wireOp",EDGE,"E62.sketch_text.stroke-110")}),-1.0]])]});
            var Q29;
            {var subQ0=sQuery(id+"F2.wireOp",EDGE,"E52");Q29=makeQuery(id+"F2.imprint","IMPRINT",FACE,{"disambiguationData":[TD([[makeQuery(id+"F2.imprint","IMPRINT",EDGE,{"derivedFrom":subQ0}),-1.0]])]});}
            var Q30;
            {var subQ0=sQuery(id+"F2.wireOp",EDGE,"E51");Q30=makeQuery(id+"F2.imprint","IMPRINT",FACE,{"disambiguationData":[TD([[makeQuery(id+"F2.imprint","IMPRINT",EDGE,{"derivedFrom":subQ0}),-1.0]])]});}
            var Q31;
            {var subQ1=sQuery(id+"F2.wireOp",EDGE,"E49");Q31=makeQuery(id+"F2.imprint","IMPRINT",FACE,{"disambiguationData":[TD([[makeQuery(id+"F2.imprint","IMPRINT",EDGE,{"derivedFrom":subQ1}),-1.0]])]});}
            var Q32;
            {var subQ0=sQuery(id+"F2.wireOp",EDGE,"E48");Q32=makeQuery(id+"F2.imprint","IMPRINT",FACE,{"disambiguationData":[TD([[makeQuery(id+"F2.imprint","IMPRINT",EDGE,{"derivedFrom":subQ0}),1.0]])]});}
            var Q33;
            {var subQ4=sQuery(id+"F2.wireOp",EDGE,"E48");Q33=makeQuery(id+"F2.imprint","IMPRINT",FACE,{"disambiguationData":[TD([[makeQuery(id+"F2.imprint","IMPRINT",EDGE,{"derivedFrom":subQ4}),-1.0]])]});}
            var Q34;
            Q34=makeQuery(id+"F2.imprint","IMPRINT",FACE,{"disambiguationData":[TD([[makeQuery(id+"F2.imprint","IMPRINT",EDGE,{"derivedFrom":sQuery(id+"F2.wireOp",EDGE,"E46")}),-1.0]])]});
            var Q35;
            Q35=makeQuery(id+"F2.imprint","IMPRINT",FACE,{"disambiguationData":[TD([[makeQuery(id+"F2.imprint","IMPRINT",EDGE,{"derivedFrom":sQuery(id+"F2.wireOp",EDGE,"E44")}),-1.0]])]});
            var Q36;
            Q36=makeQuery(id+"F2.imprint","IMPRINT",FACE,{"disambiguationData":[TD([[makeQuery(id+"F2.imprint","IMPRINT",EDGE,{"derivedFrom":sQuery(id+"F2.wireOp",EDGE,"E42")}),1.0]])]});
            var Q37;
            {var subQ0=sQuery(id+"F2.wireOp",EDGE,"E35");Q37=makeQuery(id+"F2.imprint","IMPRINT",FACE,{"disambiguationData":[TD([[makeQuery(id+"F2.imprint","IMPRINT",EDGE,{"derivedFrom":subQ0}),1.0]])]});}
            var Q38;
            Q38=makeQuery(id+"F2.imprint","IMPRINT",FACE,{"disambiguationData":[TD([[makeQuery(id+"F2.imprint","IMPRINT",EDGE,{"derivedFrom":sQuery(id+"F2.wireOp",EDGE,"E36")}),-1.0]])]});
            var Q39;
            Q39=makeQuery(id+"F2.imprint","IMPRINT",FACE,{"disambiguationData":[TD([[makeQuery(id+"F2.imprint","IMPRINT",EDGE,{"derivedFrom":sQuery(id+"F2.wireOp",EDGE,"E38")}),-1.0]])]});
            var Q40;
            Q40=makeQuery(id+"F2.imprint","IMPRINT",FACE,{"disambiguationData":[TD([[makeQuery(id+"F2.imprint","IMPRINT",EDGE,{"derivedFrom":sQuery(id+"F2.wireOp",EDGE,"E40")}),-1.0]])]});
            var Q41;
            Q41=makeQuery(id+"F2.imprint","IMPRINT",FACE,{"disambiguationData":[TD([[makeQuery(id+"F2.imprint","IMPRINT",EDGE,{"derivedFrom":sQuery(id+"F2.wireOp",EDGE,"E60.sketch_text.stroke-66")}),-1.0]])]});
            extrude(context, id + "F3", {"entities" : qUnion([Q0, Q1, Q2, Q3, Q4, Q5, Q6, Q7, Q8, Q9, Q10, Q11, Q12, Q13, Q14, Q15, Q16, Q17, Q18, Q19, Q20, Q21, Q22, Q23, Q24, Q25, Q26, Q27, Q28, Q29, Q30, Q31, Q32, Q33, Q34, Q35, Q36, Q37, Q38, Q39, Q40, Q41]), "operationType" : NewBodyOperationType.ADD, "depth" : .8 * mm, "offsetDistance" : 25 * mm});
        }
        {
            var Q0;
            Q0=makeQuery(id+"F3.opExtrude","CAP_FACE",FACE,{"disambiguationData":[OSD([sQuery(id+"F2.wireOp",EDGE,"E50"),sQuery(id+"F2.wireOp",EDGE,"E53"),sQuery(id+"F2.wireOp",EDGE,"E54"),sQuery(id+"F2.wireOp",EDGE,"E55"),sQuery(id+"F2.wireOp",EDGE,"E57"),sQuery(id+"F2.wireOp",EDGE,"E59")])],"isStart":false});
            var sketch = newSketch(context, id + "F4", { "sketchPlane" : qUnion([Q0])});
            skFitSpline(sketch, "E68", {"points": [v(1.37, -12.89) * mm, v(18.9, -24.72) * mm, v(45.4, -32.17) * mm], "startDerivative": vector(30.87, -29.73) * mm, "endDerivative": vector(47.12, -6.3) * mm});
            skFitSpline(sketch, "E69", {"points": [v(-1.98, -12.48) * mm, v(18.34, -26.68) * mm, v(45.4, -34.32) * mm], "startDerivative": vector(34.69, -38) * mm, "endDerivative": vector(48.3, -6.34) * mm});
            skFitSpline(sketch, "E70", {"points": [v(1.37, -12.89) * mm, v(22.2, -12.25) * mm, v(45.48, -7.1) * mm], "startDerivative": vector(44.38, -2.18) * mm, "endDerivative": vector(34.77, 9.05) * mm});
            skFitSpline(sketch, "E71", {"points": [v(-39.29, -25.63) * mm, v(-8.43, -23.14) * mm, v(22.66, -36.5) * mm], "startDerivative": vector(63.24, 41.09) * mm, "endDerivative": vector(60.24, -34.22) * mm});
            skFitSpline(sketch, "E72", {"points": [v(-39.29, -28.2) * mm, v(-9.86, -24.95) * mm, v(18.67, -36.5) * mm], "startDerivative": vector(58.5, 40.42) * mm, "endDerivative": vector(56.35, -26.33) * mm});
            skFitSpline(sketch, "E73", {"points": [v(-39.29, 1.8) * mm, v(-21.77, -7.9) * mm, v(-1.98, -12.48) * mm], "startDerivative": vector(51.08, -34.3) * mm, "endDerivative": vector(42.59, -4.16) * mm});
            skLineSegment(sketch, "E74", {"start": v(-39.29, -36.5) * mm, "end": v(45.4, -36.5) * mm});
            skSolve(sketch);
        }
        {
            var Q0;
            {var subQ2=sQuery(id+"F4.wireOp",EDGE,"E69");Q0=makeQuery(id+"F4.imprint","IMPRINT",FACE,{"disambiguationData":[TD([[makeQuery(id+"F4.imprint","IMPRINT",EDGE,{"derivedFrom":subQ2}),-1.0]])]});}
            var Q1;
            {var subQ0=sQuery(id+"F4.wireOp",EDGE,"E72");Q1=makeQuery(id+"F4.imprint","IMPRINT",FACE,{"disambiguationData":[TD([[makeQuery(id+"F4.imprint","IMPRINT",EDGE,{"derivedFrom":subQ0}),-1.0]])]});}
            var Q2;
            {var subQ0=sQuery(id+"F4.wireOp",EDGE,"E68");Q2=makeQuery(id+"F4.imprint","IMPRINT",FACE,{"disambiguationData":[TD([[makeQuery(id+"F4.imprint","IMPRINT",EDGE,{"derivedFrom":subQ0}),1.0]])]});}
            extrude(context, id + "F5", {"entities" : qUnion([Q0, Q1, Q2]), "operationType" : NewBodyOperationType.ADD, "depth" : .8 * mm, "offsetDistance" : 25 * mm});
        }
        {
            var Q0;
            Q0=qCreatedBy(makeId("Top.planeOp"),FACE);
            cPlane(context, id + "F6", {"entities" : qUnion([Q0]), "cplaneType" : CPlaneType.OFFSET, "offset" : .15 * mm, "width" : 150 * mm, "height" : 150 * mm});
        }
        {
            var Q0;
            Q0=qCreatedBy(id+"F6.planeOp",FACE);
            var sketch = newSketch(context, id + "F7", { "sketchPlane" : qUnion([Q0])});
            skCircle(sketch, "E75", {"center": v(3.09, 38.63) * mm, "radius": 4 * mm});
            skCircle(sketch, "E76", {"center": v(3.12, -55.18) * mm, "radius": 4 * mm});
            skSolve(sketch);
        }
        {
            var Q0;
            Q0 = qSketchRegion(id + "F7", true);
            extrude(context, id + "F8", {"entities" : qUnion([Q0]), "operationType" : NewBodyOperationType.REMOVE, "depth" : 2 * mm, "offsetDistance" : 25 * mm});
        }
    });
